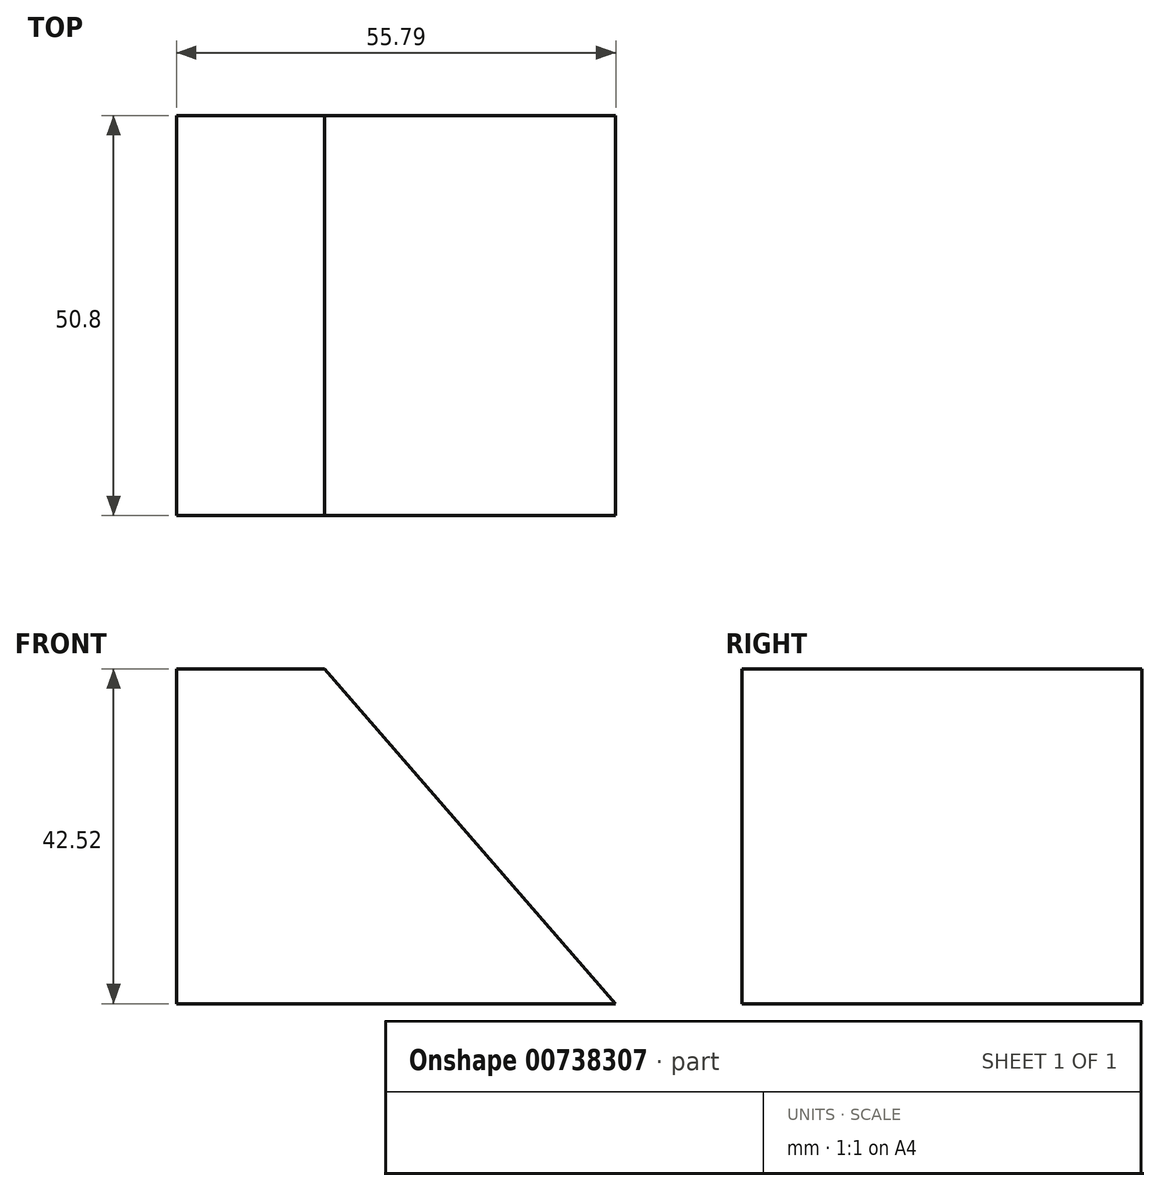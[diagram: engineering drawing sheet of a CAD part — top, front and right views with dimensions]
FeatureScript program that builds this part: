
annotation { "Feature Type Name" : "Feature", "Feature Type Description" : "" }
export const myFeature = defineFeature(function(context is Context, id is Id, definition is map)
    precondition{}
    {
        {
            var Q0;
            Q0=qCreatedBy(makeId("Front.planeOp"),FACE);
            var sketch = newSketch(context, id + "F0", { "sketchPlane" : qUnion([Q0])});
            skLineSegment(sketch, "E0", {"start": v(0, 0) * mm, "end": v(0, 42.52) * mm});
            skLineSegment(sketch, "E1", {"start": v(0, 42.52) * mm, "end": v(55.79, 42.52) * mm});
            skLineSegment(sketch, "E2", {"start": v(55.79, 42.52) * mm, "end": v(55.79, 0) * mm});
            skLineSegment(sketch, "E3", {"start": v(55.79, 0) * mm, "end": v(0, 0) * mm});
            skSolve(sketch);
        }
        {
            var Q0;
            Q0=makeQuery(id+"F0.imprint","IMPRINT",FACE,{"disambiguationData":[TD([[makeQuery(id+"F0.imprint","IMPRINT",EDGE,{"derivedFrom":sQuery(id+"F0.wireOp",EDGE,"E0")}),-1.0]])]});
            extrude(context, id + "F1", {"entities" : qUnion([Q0]), "depth" : 25.4 * mm, "offsetDistance" : 25.4 * mm});
        }
        {
            var Q0;
            Q0=makeQuery(id+"F1.opExtrude","CAP_FACE",FACE,{"disambiguationData":[OSD([sQuery(id+"F0.wireOp",EDGE,"E0"),sQuery(id+"F0.wireOp",EDGE,"E1"),sQuery(id+"F0.wireOp",EDGE,"E2"),sQuery(id+"F0.wireOp",EDGE,"E3")])],"isStart":false});
            extrude(context, id + "F2", {"entities" : qUnion([Q0]), "operationType" : NewBodyOperationType.ADD, "depth" : 25.4 * mm, "offsetDistance" : 25.4 * mm});
        }
        {
            var Q0;
            Q0=makeQuery(id+"F2.opExtrude","CAP_FACE",FACE,{"disambiguationData":[OSD([sQuery(id+"F0.wireOp",EDGE,"E0"),sQuery(id+"F0.wireOp",EDGE,"E1"),sQuery(id+"F0.wireOp",EDGE,"E2"),sQuery(id+"F0.wireOp",EDGE,"E3")])],"isStart":false});
            var sketch = newSketch(context, id + "F3", { "sketchPlane" : qUnion([Q0])});
            skLineSegment(sketch, "E4", {"start": v(18.8, 42.52) * mm, "end": v(55.79, 0) * mm});
            skSolve(sketch);
        }
        {
            var Q0;
            {var subQ0=sQuery(id+"F3.wireOp",EDGE,"E4");Q0=makeQuery(id+"F3.imprint","IMPRINT",FACE,{"disambiguationData":[TD([[makeQuery(id+"F3.imprint","IMPRINT",EDGE,{"derivedFrom":subQ0}),1.0]])]});}
            extrude(context, id + "F4", {"entities" : qUnion([Q0]), "operationType" : NewBodyOperationType.REMOVE, "oppositeDirection" : true, "depth" : 25.4 * mm, "offsetDistance" : 25.4 * mm});
        }
        {
            var Q0;
            Q0=makeQuery(id+"F4.boolean.opBoolean","COPY",FACE,{"derivedFrom":makeQuery(id+"F4.opExtrude","CAP_FACE",FACE,{"disambiguationData":[OSD([sQuery(id+"F0.wireOp",EDGE,"E1"),sQuery(id+"F0.wireOp",EDGE,"E2"),sQuery(id+"F3.wireOp",EDGE,"E4")])],"isStart":false})});
            extrude(context, id + "F5", {"entities" : qUnion([Q0]), "operationType" : NewBodyOperationType.REMOVE, "oppositeDirection" : true, "depth" : 25.4 * mm, "offsetDistance" : 25.4 * mm});
        }
    });
